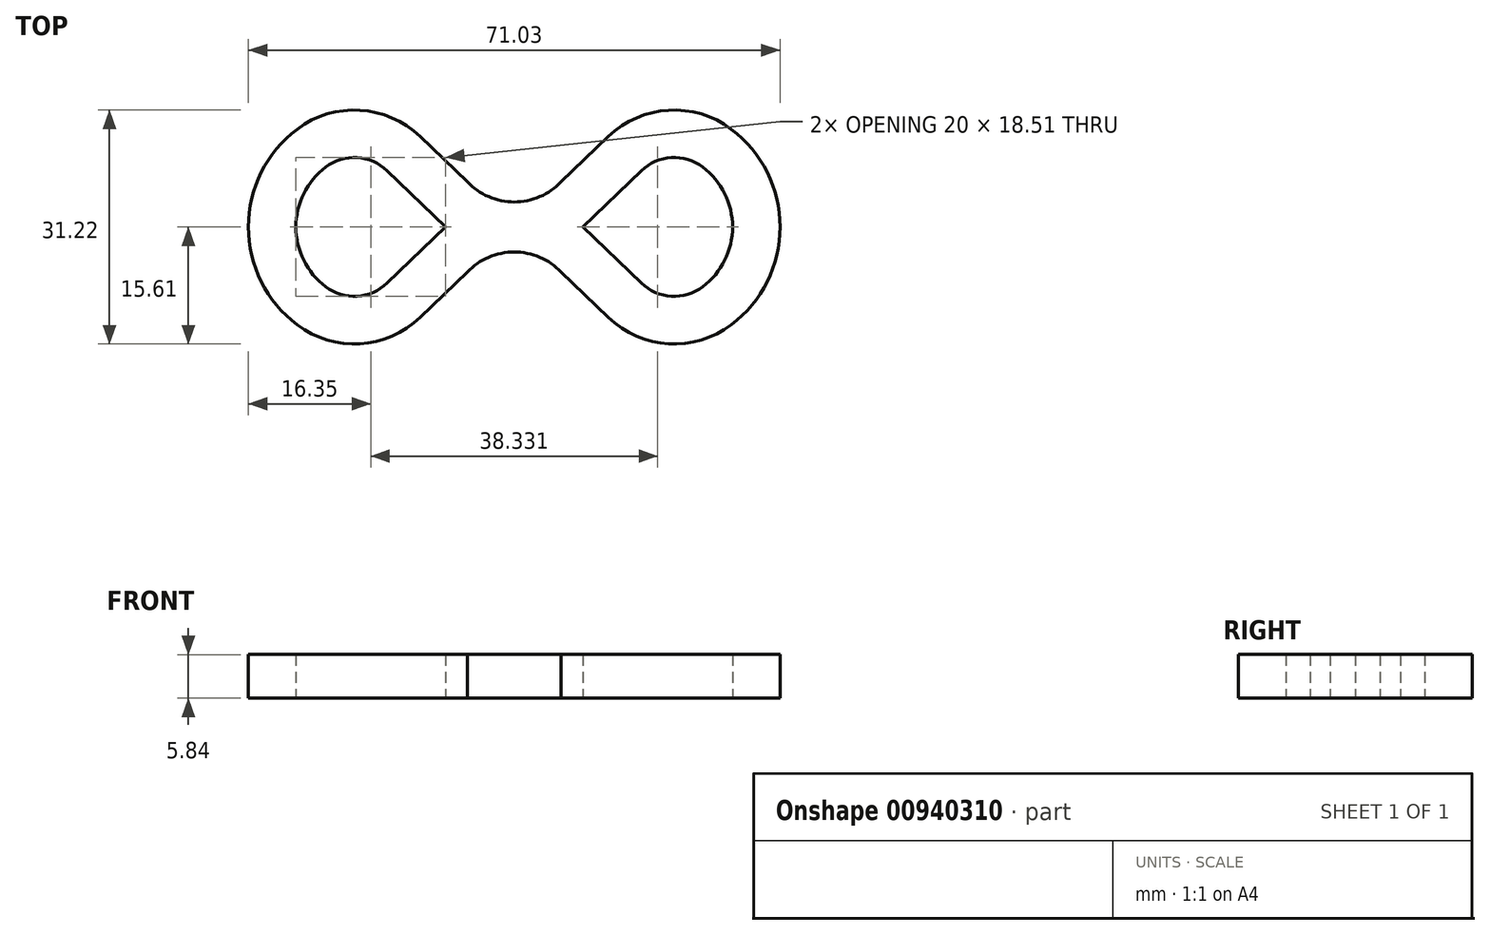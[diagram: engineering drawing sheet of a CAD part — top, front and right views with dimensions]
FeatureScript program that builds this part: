
annotation { "Feature Type Name" : "Feature", "Feature Type Description" : "" }
export const myFeature = defineFeature(function(context is Context, id is Id, definition is map)
    precondition{}
    {
        {
            var Q0;
            Q0=qCreatedBy(makeId("Top.planeOp"),FACE);
            var sketch = newSketch(context, id + "F0", { "sketchPlane" : qUnion([Q0])});
            skArc(sketch, "E0", {"start": v(-16.02, 7.98) * mm, "mid": v(-18.95, 4.46) * mm, "end": v(-20, 0) * mm});
            skLineSegment(sketch, "E1", {"start": v(-7.8, 7.5) * mm, "end": v(0, 0) * mm});
            skPoint(sketch, "E2.visualSharp", {"position": v(-10.4, 10) * mm});
            skArc(sketch, "E2.filletArc", {"start": v(-7.8, 7.5) * mm, "mid": v(-11.82, 9.25) * mm, "end": v(-16.02, 7.98) * mm});
            skArc(sketch, "E3.MirrorCS", {"start": v(-16.02, -7.98) * mm, "mid": v(-18.95, -4.46) * mm, "end": v(-20, 0) * mm});
            skArc(sketch, "E4.MirrorCS", {"start": v(-7.8, -7.5) * mm, "mid": v(-11.82, -9.25) * mm, "end": v(-16.02, -7.98) * mm});
            skLineSegment(sketch, "E5.MirrorCS", {"start": v(-7.8, -7.5) * mm, "end": v(0, 0) * mm});
            skLineSegment(sketch, "E6.0", {"start": v(-3.4, 12.07) * mm, "end": v(3.44, 5.5) * mm});
            skArc(sketch, "E6.1", {"start": v(-19.85, 13.05) * mm, "mid": v(-24.63, 7.3) * mm, "end": v(-26.35, 0) * mm});
            skArc(sketch, "E6.2", {"start": v(-19.85, -13.05) * mm, "mid": v(-24.63, -7.3) * mm, "end": v(-26.35, 0) * mm});
            skArc(sketch, "E6.3", {"start": v(-3.4, 12.07) * mm, "mid": v(-11.44, 15.6) * mm, "end": v(-19.85, 13.05) * mm});
            skArc(sketch, "E6.4", {"start": v(-3.4, -12.07) * mm, "mid": v(-11.44, -15.6) * mm, "end": v(-19.85, -13.05) * mm});
            skLineSegment(sketch, "E6.5", {"start": v(-3.4, -12.07) * mm, "end": v(3.44, -5.5) * mm});
            skPoint(sketch, "E7", {"position": v(9.17, 0) * mm});
            skArc(sketch, "E8.MirrorCS", {"start": v(21.73, -12.07) * mm, "mid": v(29.77, -15.6) * mm, "end": v(38.18, -13.05) * mm});
            skArc(sketch, "E9.MirrorCS", {"start": v(21.73, 12.07) * mm, "mid": v(29.77, 15.6) * mm, "end": v(38.18, 13.05) * mm});
            skArc(sketch, "E10.MirrorCS", {"start": v(38.18, -13.05) * mm, "mid": v(42.96, -7.3) * mm, "end": v(44.68, 0) * mm});
            skLineSegment(sketch, "E11.MirrorCS", {"start": v(21.73, -12.07) * mm, "end": v(14.9, -5.5) * mm});
            skPoint(sketch, "E12.MirrorP", {"position": v(28.73, 10) * mm});
            skArc(sketch, "E13.MirrorCS", {"start": v(38.18, 13.05) * mm, "mid": v(42.96, 7.3) * mm, "end": v(44.68, 0) * mm});
            skLineSegment(sketch, "E14.MirrorCS", {"start": v(21.73, 12.07) * mm, "end": v(14.9, 5.5) * mm});
            skLineSegment(sketch, "E15.MirrorCS", {"start": v(26.13, -7.5) * mm, "end": v(18.33, 0) * mm});
            skArc(sketch, "E16.MirrorCS", {"start": v(26.13, -7.5) * mm, "mid": v(30.15, -9.25) * mm, "end": v(34.35, -7.98) * mm});
            skArc(sketch, "E17.MirrorCS", {"start": v(34.35, -7.98) * mm, "mid": v(37.28, -4.46) * mm, "end": v(38.33, 0) * mm});
            skArc(sketch, "E18.MirrorCS", {"start": v(26.13, 7.5) * mm, "mid": v(30.15, 9.25) * mm, "end": v(34.35, 7.98) * mm});
            skLineSegment(sketch, "E19.MirrorCS", {"start": v(26.13, 7.5) * mm, "end": v(18.33, 0) * mm});
            skArc(sketch, "E20.MirrorCS", {"start": v(34.35, 7.98) * mm, "mid": v(37.28, 4.46) * mm, "end": v(38.33, 0) * mm});
            skArc(sketch, "E21", {"start": v(2.88, 6.04) * mm, "mid": v(9.17, 3.34) * mm, "end": v(15.45, 6.04) * mm});
            skArc(sketch, "E22.MirrorCS", {"start": v(2.88, -6.04) * mm, "mid": v(9.17, -3.34) * mm, "end": v(15.45, -6.04) * mm});
            skSolve(sketch);
        }
        {
            var Q0;
            Q0=makeQuery(id+"F0.imprint","IMPRINT",FACE,{"disambiguationData":[TD([[makeQuery(id+"F0.imprint","IMPRINT",EDGE,{"derivedFrom":sQuery(id+"F0.wireOp",EDGE,"E0")}),-1.0]])]});
            extrude(context, id + "F1", {"entities" : qUnion([Q0]), "depth" : 5.84 * mm, "offsetDistance" : 25.4 * mm});
        }
    });
